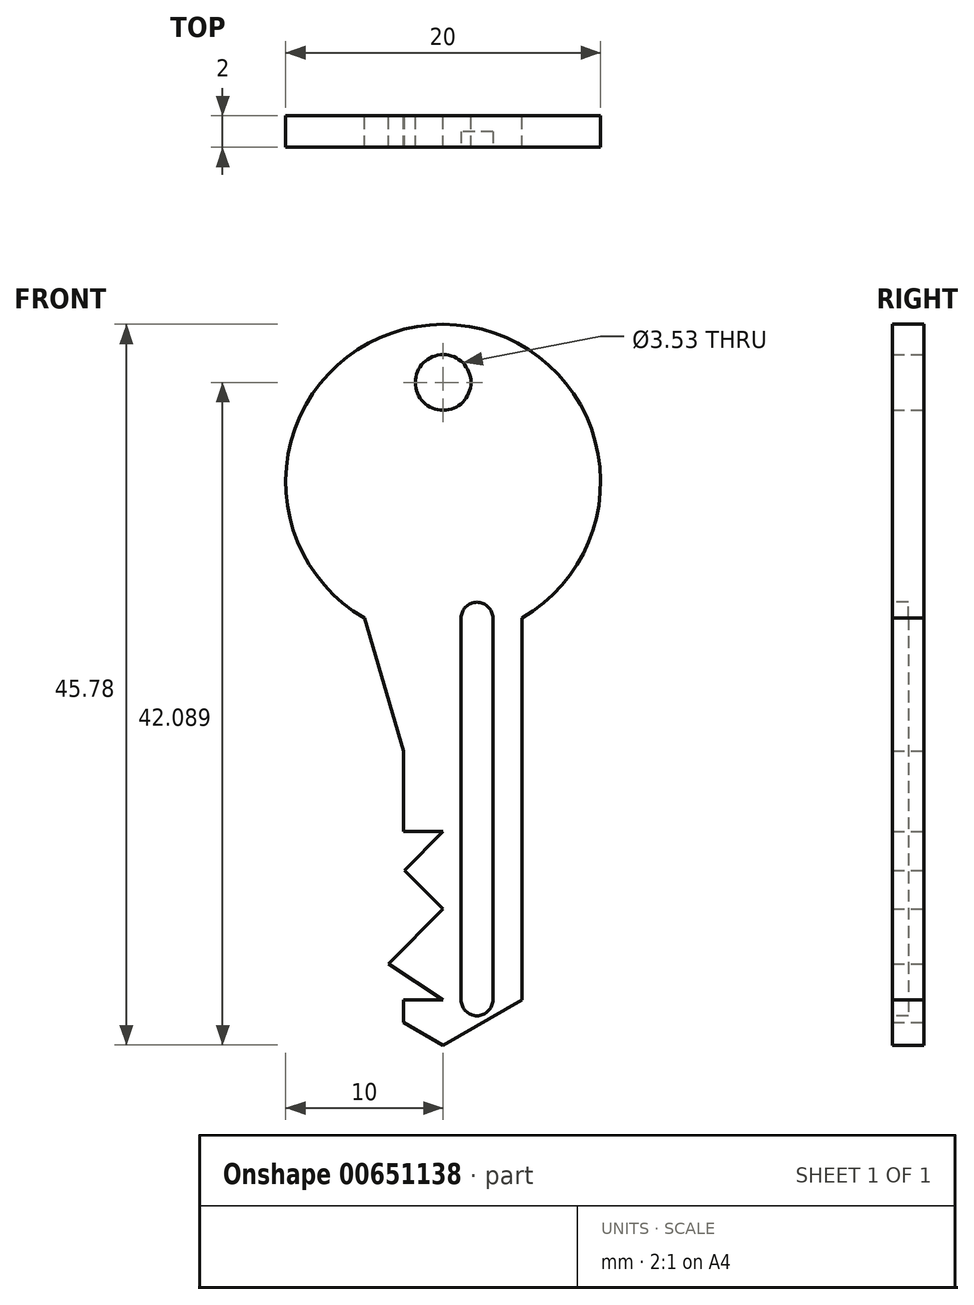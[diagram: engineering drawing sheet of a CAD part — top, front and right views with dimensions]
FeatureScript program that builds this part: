
annotation { "Feature Type Name" : "Feature", "Feature Type Description" : "" }
export const myFeature = defineFeature(function(context is Context, id is Id, definition is map)
    precondition{}
    {
        {
            var Q0;
            Q0=qCreatedBy(makeId("Front.planeOp"),FACE);
            var sketch = newSketch(context, id + "F0", { "sketchPlane" : qUnion([Q0])});
            skArc(sketch, "E0", {"start": v(5, -8.66) * mm, "mid": v(0, 10) * mm, "end": v(-5, -8.66) * mm});
            skLineSegment(sketch, "E1", {"start": v(5, -32.9) * mm, "end": v(5, -8.66) * mm});
            skLineSegment(sketch, "E2", {"start": v(0, -35.78) * mm, "end": v(-2.5, -34.35) * mm});
            skLineSegment(sketch, "E3", {"start": v(0, -35.78) * mm, "end": v(5, -32.9) * mm});
            skPoint(sketch, "E4.endSnap0", {"position": v(0, -22.22) * mm});
            skLineSegment(sketch, "E5", {"start": v(-2.5, -17.1) * mm, "end": v(-2.5, -22.22) * mm});
            skLineSegment(sketch, "E6", {"start": v(-2.5, -22.22) * mm, "end": v(0, -22.22) * mm});
            skLineSegment(sketch, "E7", {"start": v(0, -22.22) * mm, "end": v(-2.46, -24.68) * mm});
            skLineSegment(sketch, "E8", {"start": v(-2.46, -24.68) * mm, "end": v(0, -27.14) * mm});
            skLineSegment(sketch, "E9", {"start": v(0, -27.14) * mm, "end": v(-3.47, -30.6) * mm});
            skLineSegment(sketch, "E10", {"start": v(-3.47, -30.6) * mm, "end": v(0, -32.9) * mm});
            skLineSegment(sketch, "E11", {"start": v(0, -32.9) * mm, "end": v(-2.5, -32.9) * mm});
            skLineSegment(sketch, "E12", {"start": v(-5, -8.66) * mm, "end": v(-2.5, -17.1) * mm});
            skLineSegment(sketch, "E13", {"start": v(-2.5, -32.9) * mm, "end": v(-2.5, -34.35) * mm});
            skCircle(sketch, "E14", {"center": v(0, 6.3) * mm, "radius": 1.77 * mm});
            skSolve(sketch);
        }
        {
            var Q0;
            Q0=makeQuery(id+"F0.imprint","IMPRINT",FACE,{"disambiguationData":[TD([[makeQuery(id+"F0.imprint","IMPRINT",EDGE,{"derivedFrom":sQuery(id+"F0.wireOp",EDGE,"E0")}),1.0]])]});
            extrude(context, id + "F1", {"entities" : qUnion([Q0]), "endBound" : BoundingType.SYMMETRIC, "depth" : 2 * mm, "offsetDistance" : 25.4 * mm});
        }
        {
            var Q0;
            Q0=makeQuery(id+"F1.opExtrude","CAP_FACE",FACE,{"disambiguationData":[OSD([sQuery(id+"F0.wireOp",EDGE,"E0"),sQuery(id+"F0.wireOp",EDGE,"E1"),sQuery(id+"F0.wireOp",EDGE,"E2"),sQuery(id+"F0.wireOp",EDGE,"E3"),sQuery(id+"F0.wireOp",EDGE,"E5"),sQuery(id+"F0.wireOp",EDGE,"E6"),sQuery(id+"F0.wireOp",EDGE,"E7"),sQuery(id+"F0.wireOp",EDGE,"E8"),sQuery(id+"F0.wireOp",EDGE,"E9"),sQuery(id+"F0.wireOp",EDGE,"E10"),sQuery(id+"F0.wireOp",EDGE,"E11"),sQuery(id+"F0.wireOp",EDGE,"E12"),sQuery(id+"F0.wireOp",EDGE,"E13"),sQuery(id+"F0.wireOp",EDGE,"E14")])],"isStart":false});
            var sketch = newSketch(context, id + "F2", { "sketchPlane" : qUnion([Q0])});
            skLineSegment(sketch, "E15.left", {"start": v(3.16, -8.66) * mm, "end": v(3.16, -32.9) * mm});
            skLineSegment(sketch, "E15.right", {"start": v(1.14, -8.66) * mm, "end": v(1.14, -32.9) * mm});
            skArc(sketch, "E16", {"start": v(3.16, -8.66) * mm, "mid": v(2.15, -7.65) * mm, "end": v(1.14, -8.66) * mm});
            skArc(sketch, "E17", {"start": v(1.14, -32.9) * mm, "mid": v(2.15, -33.92) * mm, "end": v(3.16, -32.9) * mm});
            skSolve(sketch);
        }
        {
            var Q0;
            Q0=makeQuery(id+"F2.imprint","IMPRINT",FACE,{"disambiguationData":[TD([[makeQuery(id+"F2.imprint","IMPRINT",EDGE,{"derivedFrom":sQuery(id+"F2.wireOp",EDGE,"E15.left")}),-1.0]])]});
            extrude(context, id + "F3", {"entities" : qUnion([Q0]), "operationType" : NewBodyOperationType.REMOVE, "oppositeDirection" : true, "depth" : 1 * mm, "offsetDistance" : 25.4 * mm});
        }
    });
